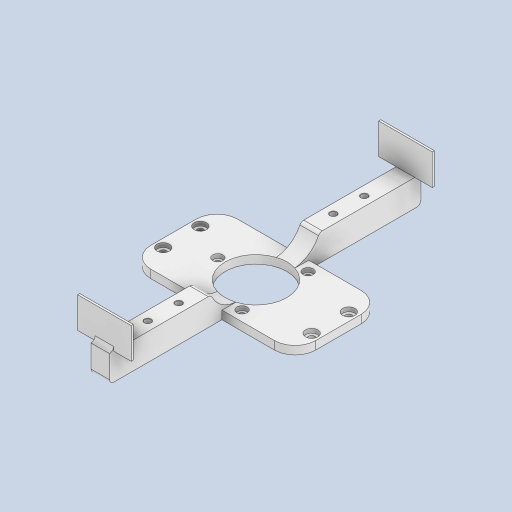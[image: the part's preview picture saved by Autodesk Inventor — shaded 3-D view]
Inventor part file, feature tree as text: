
AUTODESK INVENTOR PART (.ipt)
format: ipt  version: 2023 (Build 270158000, 158)  size: 368,128 bytes
history: native  units: in
note: dims shown in document units (in); Inventor stores cm internally (conversion verified against a paired STEP export)
features: other x5, extrude x4, sketch x4, fillet x3, mirror x2, hole x2, chamfer x1
ambient origin geometry x8: Origin, YZ Plane, XZ Plane, XY Plane, X Axis, Y Axis, Z Axis, Center Point
bodies: Body1 (feature_tree), Body2 (feature_tree)
feature tree (21):
  other  "GIM3505-8_with-driver.ipt"
  other  "ソリッド1"
  extrude  "押し出し1"  Depth=0.3937in
  extrude  "押し出し2"  Depth=0.1063in
  mirror  "ミラー1"
  extrude  "押し出し3"  Depth=1.1811in TaperAngle=360.0deg
  mirror  "ミラー2"
  fillet  "フィレット1"  Radius=0.3543in
  fillet  "フィレット2"  Radius=0.1772in
  sketch  "スケッチ4"
  hole  "穴1"  [1 undecoded]
  hole  "穴2"  [1 undecoded]
  extrude  "押し出し4"  Depth=3.1496in
  fillet  "フィレット3"  Radius=0.3543in
  chamfer  "面取り1"  Distance=1.4173in
  other  "TaggingFeature1"
  sketch  "スケッチ2"
  sketch  "スケッチ3"
  sketch  "スケッチ5"
  other  "ソリッド1::GIM3505-8_with-driver.ipt"
  other  "Srf1"
note: 2 required parameter values undecoded (feature->parameter linkage not recoverable at this tier; creation-order binding heuristic only, values carry confidence <= 0.55)
